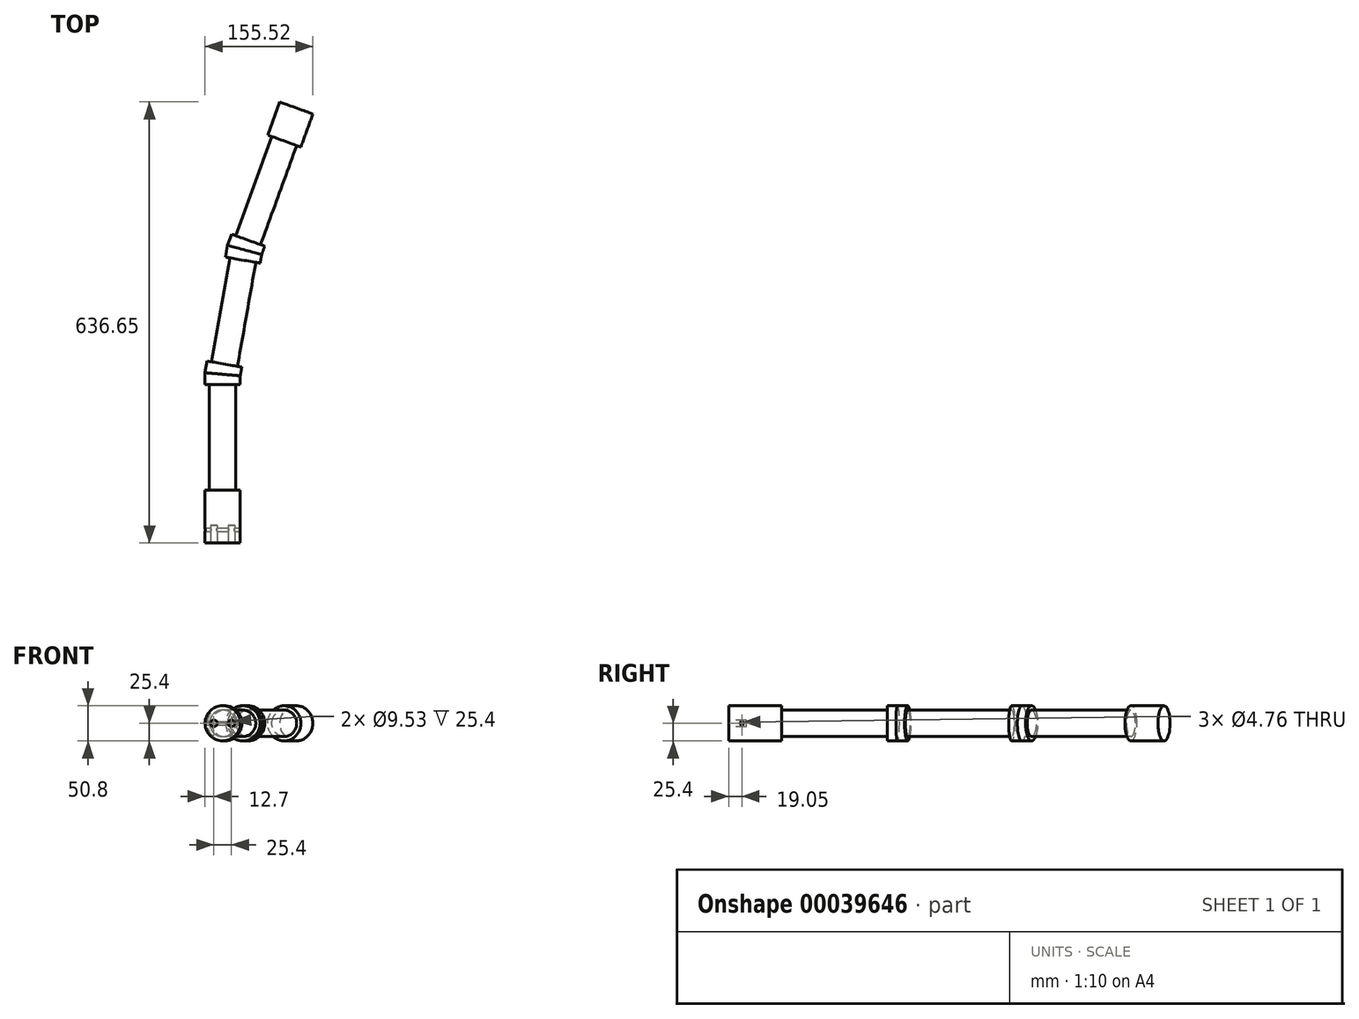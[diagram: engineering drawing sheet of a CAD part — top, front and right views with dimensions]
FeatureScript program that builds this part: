
annotation { "Feature Type Name" : "Feature", "Feature Type Description" : "" }
export const myFeature = defineFeature(function(context is Context, id is Id, definition is map)
    precondition{}
    {
        {
            var Q0;
            Q0=qCreatedBy(makeId("Top.planeOp"),FACE);
            var sketch = newSketch(context, id + "F0", { "sketchPlane" : qUnion([Q0])});
            skLineSegment(sketch, "E0", {"start": v(0, 0) * mm, "end": v(-19.05, 0) * mm});
            skLineSegment(sketch, "E1", {"start": v(0, 0) * mm, "end": v(19.05, 0) * mm});
            skLineSegment(sketch, "E2", {"start": v(19.05, 0) * mm, "end": v(19.05, 152.4) * mm});
            skLineSegment(sketch, "E3", {"start": v(-19.05, 0) * mm, "end": v(-19.05, 152.4) * mm});
            skLineSegment(sketch, "E4", {"start": v(-19.05, 152.4) * mm, "end": v(19.05, 152.4) * mm});
            skLineSegment(sketch, "E5", {"start": v(19.05, 152.4) * mm, "end": v(25.4, 152.4) * mm});
            skLineSegment(sketch, "E6", {"start": v(25.4, 152.4) * mm, "end": v(25.4, 165.1) * mm});
            skLineSegment(sketch, "E7", {"start": v(25.4, 165.1) * mm, "end": v(27.6, 177.6) * mm});
            skLineSegment(sketch, "E8", {"start": v(-19.05, 152.4) * mm, "end": v(-25.4, 152.4) * mm});
            skLineSegment(sketch, "E9", {"start": v(27.6, 177.6) * mm, "end": v(-22.42, 186.43) * mm});
            skLineSegment(sketch, "E10", {"start": v(25.4, 165.1) * mm, "end": v(-25.4, 169.54) * mm});
            skLineSegment(sketch, "E11", {"start": v(-25.4, 152.4) * mm, "end": v(-25.4, 169.54) * mm});
            skLineSegment(sketch, "E12", {"start": v(-25.4, 169.54) * mm, "end": v(-22.42, 186.43) * mm});
            skLineSegment(sketch, "E13", {"start": v(27.6, 177.6) * mm, "end": v(21.35, 178.7) * mm});
            skLineSegment(sketch, "E14", {"start": v(21.35, 178.7) * mm, "end": v(47.82, 328.8) * mm});
            skLineSegment(sketch, "E15", {"start": v(47.82, 328.8) * mm, "end": v(10.3, 335.41) * mm});
            skLineSegment(sketch, "E16", {"start": v(10.3, 335.41) * mm, "end": v(-16.17, 185.33) * mm});
            skLineSegment(sketch, "E17", {"start": v(47.82, 328.8) * mm, "end": v(54.07, 327.7) * mm});
            skLineSegment(sketch, "E18", {"start": v(54.07, 327.7) * mm, "end": v(56.27, 340.2) * mm});
            skLineSegment(sketch, "E19", {"start": v(10.3, 335.41) * mm, "end": v(4.04, 336.51) * mm});
            skLineSegment(sketch, "E20", {"start": v(56.27, 340.2) * mm, "end": v(60.62, 352.13) * mm});
            skLineSegment(sketch, "E21", {"start": v(60.62, 352.13) * mm, "end": v(12.88, 369.5) * mm});
            skLineSegment(sketch, "E22", {"start": v(56.27, 340.2) * mm, "end": v(7.02, 353.4) * mm});
            skLineSegment(sketch, "E23", {"start": v(4.04, 336.51) * mm, "end": v(7.02, 353.4) * mm});
            skLineSegment(sketch, "E24", {"start": v(7.02, 353.4) * mm, "end": v(12.88, 369.5) * mm});
            skLineSegment(sketch, "E25", {"start": v(60.62, 352.13) * mm, "end": v(54.65, 354.3) * mm});
            skLineSegment(sketch, "E26", {"start": v(19.05, 0) * mm, "end": v(25.4, 0) * mm});
            skLineSegment(sketch, "E27", {"start": v(25.4, 0) * mm, "end": v(25.4, -50.8) * mm});
            skLineSegment(sketch, "E28", {"start": v(25.4, -50.8) * mm, "end": v(-25.4, -50.8) * mm});
            skLineSegment(sketch, "E29", {"start": v(-25.4, -50.8) * mm, "end": v(-25.4, 0) * mm});
            skLineSegment(sketch, "E30", {"start": v(-25.4, 0) * mm, "end": v(-19.05, 0) * mm});
            skLineSegment(sketch, "E31", {"start": v(54.65, 354.3) * mm, "end": v(106.78, 497.51) * mm});
            skLineSegment(sketch, "E32", {"start": v(106.78, 497.51) * mm, "end": v(112.74, 495.34) * mm});
            skLineSegment(sketch, "E33", {"start": v(130.12, 543.08) * mm, "end": v(82.38, 560.45) * mm});
            skLineSegment(sketch, "E34", {"start": v(70.97, 510.54) * mm, "end": v(18.85, 367.34) * mm});
            skLineSegment(sketch, "E35", {"start": v(70.97, 510.54) * mm, "end": v(106.78, 497.51) * mm});
            skLineSegment(sketch, "E36", {"start": v(130.12, 543.08) * mm, "end": v(112.74, 495.34) * mm});
            skLineSegment(sketch, "E37", {"start": v(82.38, 560.45) * mm, "end": v(65, 512.72) * mm});
            skLineSegment(sketch, "E38", {"start": v(65, 512.72) * mm, "end": v(70.97, 510.54) * mm});
            skSolve(sketch);
        }
        {
            var Q0;
            Q0=makeQuery(id+"F0.imprint","IMPRINT",FACE,{"disambiguationData":[TD([[makeQuery(id+"F0.imprint","IMPRINT",EDGE,{"derivedFrom":sQuery(id+"F0.wireOp",EDGE,"E20")}),1.0]])]});
            var Q1;
            Q1=makeQuery(id+"F0.imprint","IMPRINT",FACE,{"disambiguationData":[TD([[makeQuery(id+"F0.imprint","IMPRINT",EDGE,{"derivedFrom":sQuery(id+"F0.wireOp",EDGE,"E15")}),-1.0]])]});
            var Q2;
            Q2=makeQuery(id+"F0.imprint","IMPRINT",FACE,{"disambiguationData":[TD([[makeQuery(id+"F0.imprint","IMPRINT",EDGE,{"derivedFrom":sQuery(id+"F0.wireOp",EDGE,"E7")}),1.0]])]});
            var Q3;
            Q3=makeQuery(id+"F0.imprint","IMPRINT",FACE,{"disambiguationData":[TD([[makeQuery(id+"F0.imprint","IMPRINT",EDGE,{"derivedFrom":sQuery(id+"F0.wireOp",EDGE,"E4")}),1.0]])]});
            var Q4;
            Q4=makeQuery(id+"F0.imprint","IMPRINT",FACE,{"disambiguationData":[TD([[makeQuery(id+"F0.imprint","IMPRINT",EDGE,{"derivedFrom":sQuery(id+"F0.wireOp",EDGE,"E0")}),1.0]])]});
            var Q5;
            Q5=makeQuery(id+"F0.imprint","IMPRINT",FACE,{"disambiguationData":[TD([[makeQuery(id+"F0.imprint","IMPRINT",EDGE,{"derivedFrom":sQuery(id+"F0.wireOp",EDGE,"4362853a-bfab-4841-ad33-0da4945ce7d8")}),-1.0]])]});
            var Q6;
            Q6=makeQuery(id+"F0.imprint","IMPRINT",FACE,{"disambiguationData":[TD([[makeQuery(id+"F0.imprint","IMPRINT",EDGE,{"derivedFrom":sQuery(id+"F0.wireOp",EDGE,"9ec19a48-1b8f-4e76-9588-66d74d53f144")}),-1.0]])]});
            var Q7;
            Q7=makeQuery(id+"F0.imprint","IMPRINT",FACE,{"disambiguationData":[TD([[makeQuery(id+"F0.imprint","IMPRINT",EDGE,{"derivedFrom":sQuery(id+"F0.wireOp",EDGE,"E32")}),1.0]])]});
            var Q8;
            Q8=makeQuery(id+"F0.imprint","IMPRINT",FACE,{"disambiguationData":[TD([[makeQuery(id+"F0.imprint","IMPRINT",EDGE,{"derivedFrom":sQuery(id+"F0.wireOp",EDGE,"134bd195-3179-4c87-b82c-456532974db7")}),1.0]])]});
            var Q9;
            Q9=makeQuery(id+"F0.imprint","IMPRINT",FACE,{"disambiguationData":[TD([[makeQuery(id+"F0.imprint","IMPRINT",EDGE,{"derivedFrom":sQuery(id+"F0.wireOp",EDGE,"030bf412-2708-412a-a3c6-39b4ca16a0eb")}),1.0]])]});
            var Q10;
            Q10=makeQuery(id+"F0.imprint","IMPRINT",FACE,{"disambiguationData":[TD([[makeQuery(id+"F0.imprint","IMPRINT",EDGE,{"derivedFrom":sQuery(id+"F0.wireOp",EDGE,"134bd195-3179-4c87-b82c-456532974db7")}),-1.0]])]});
            var Q11;
            Q11=makeQuery(id+"F0.imprint","IMPRINT",FACE,{"disambiguationData":[TD([[makeQuery(id+"F0.imprint","IMPRINT",EDGE,{"derivedFrom":sQuery(id+"F0.wireOp",EDGE,"E33")}),-1.0]])]});
            var Q12;
            Q12=makeQuery(id+"F0.imprint","IMPRINT",FACE,{"disambiguationData":[TD([[makeQuery(id+"F0.imprint","IMPRINT",EDGE,{"derivedFrom":sQuery(id+"F0.wireOp",EDGE,"e989e8fa-5b56-48d0-8351-93b8a3e71791")}),-1.0]])]});
            extrude(context, id + "F1", {"entities" : qUnion([Q0, Q1, Q2, Q3, Q4, Q5, Q6, Q7, Q8, Q9, Q10, Q11, Q12]), "endBound" : BoundingType.SYMMETRIC, "depth" : 50.8 * mm});
        }
        {
            var Q0;
            {var subQ1=sQuery(id+"F0.wireOp",EDGE,"E31");Q0=makeQuery(id+"F0.imprint","IMPRINT",FACE,{"disambiguationData":[TD([[makeQuery(id+"F0.imprint","IMPRINT",EDGE,{"derivedFrom":subQ1}),1.0]])]});}
            var Q1;
            {var subQ1=sQuery(id+"F0.wireOp",EDGE,"E14");Q1=makeQuery(id+"F0.imprint","IMPRINT",FACE,{"disambiguationData":[TD([[makeQuery(id+"F0.imprint","IMPRINT",EDGE,{"derivedFrom":subQ1}),1.0]])]});}
            var Q2;
            Q2=makeQuery(id+"F0.imprint","IMPRINT",FACE,{"disambiguationData":[TD([[makeQuery(id+"F0.imprint","IMPRINT",EDGE,{"derivedFrom":sQuery(id+"F0.wireOp",EDGE,"E0")}),-1.0]])]});
            extrude(context, id + "F2", {"entities" : qUnion([Q0, Q1, Q2]), "endBound" : BoundingType.SYMMETRIC, "depth" : 38.1 * mm});
        }
        {
            var Q0;
            Q0=makeQuery(id+"F2.opExtrude","CAP_EDGE",EDGE,{"disambiguationData":[OSD([sQuery(id+"F0.wireOp",EDGE,"E31")])],"isStart":false});
            var Q1;
            Q1=makeQuery(id+"F2.opExtrude","CAP_EDGE",EDGE,{"disambiguationData":[OSD([sQuery(id+"F0.wireOp",EDGE,"E34")])],"isStart":false});
            var Q2;
            Q2=makeQuery(id+"F2.opExtrude","CAP_EDGE",EDGE,{"disambiguationData":[OSD([sQuery(id+"F0.wireOp",EDGE,"E14")])],"isStart":false});
            var Q3;
            Q3=makeQuery(id+"F2.opExtrude","CAP_EDGE",EDGE,{"disambiguationData":[OSD([sQuery(id+"F0.wireOp",EDGE,"E16")])],"isStart":false});
            var Q4;
            Q4=makeQuery(id+"F2.opExtrude","CAP_EDGE",EDGE,{"disambiguationData":[OSD([sQuery(id+"F0.wireOp",EDGE,"E2")])],"isStart":false});
            var Q5;
            Q5=makeQuery(id+"F2.opExtrude","CAP_EDGE",EDGE,{"disambiguationData":[OSD([sQuery(id+"F0.wireOp",EDGE,"E3")])],"isStart":false});
            var Q6;
            Q6=makeQuery(id+"F2.opExtrude","CAP_EDGE",EDGE,{"disambiguationData":[OSD([sQuery(id+"F0.wireOp",EDGE,"E2")])],"isStart":true});
            var Q7;
            Q7=makeQuery(id+"F2.opExtrude","CAP_EDGE",EDGE,{"disambiguationData":[OSD([sQuery(id+"F0.wireOp",EDGE,"E3")])],"isStart":true});
            var Q8;
            Q8=makeQuery(id+"F2.opExtrude","CAP_EDGE",EDGE,{"disambiguationData":[OSD([sQuery(id+"F0.wireOp",EDGE,"E14")])],"isStart":true});
            var Q9;
            Q9=makeQuery(id+"F2.opExtrude","CAP_EDGE",EDGE,{"disambiguationData":[OSD([sQuery(id+"F0.wireOp",EDGE,"E16")])],"isStart":true});
            var Q10;
            Q10=makeQuery(id+"F2.opExtrude","CAP_EDGE",EDGE,{"disambiguationData":[OSD([sQuery(id+"F0.wireOp",EDGE,"E31")])],"isStart":true});
            var Q11;
            Q11=makeQuery(id+"F2.opExtrude","CAP_EDGE",EDGE,{"disambiguationData":[OSD([sQuery(id+"F0.wireOp",EDGE,"E34")])],"isStart":true});
            fillet(context, id + "F3", {"entities" : qUnion([Q0, Q1, Q2, Q3, Q4, Q5, Q6, Q7, Q8, Q9, Q10, Q11]), "radius" : 19.05 * mm, "tangentPropagation" : true, "allowEdgeOverflow" : false});
        }
        {
            var Q0;
            Q0=makeQuery(id+"F1.opExtrude","CAP_EDGE",EDGE,{"disambiguationData":[OSD([sQuery(id+"F0.wireOp",EDGE,"E7")])],"isStart":false});
            var Q1;
            Q1=makeQuery(id+"F1.opExtrude","CAP_EDGE",EDGE,{"disambiguationData":[OSD([sQuery(id+"F0.wireOp",EDGE,"E12")])],"isStart":false});
            var Q2;
            Q2=makeQuery(id+"F1.opExtrude","CAP_EDGE",EDGE,{"disambiguationData":[OSD([sQuery(id+"F0.wireOp",EDGE,"E11")])],"isStart":false});
            var Q3;
            Q3=makeQuery(id+"F1.opExtrude","CAP_EDGE",EDGE,{"disambiguationData":[OSD([sQuery(id+"F0.wireOp",EDGE,"E6")])],"isStart":false});
            var Q4;
            Q4=makeQuery(id+"F1.opExtrude","CAP_EDGE",EDGE,{"disambiguationData":[OSD([sQuery(id+"F0.wireOp",EDGE,"E7")])],"isStart":true});
            var Q5;
            Q5=makeQuery(id+"F1.opExtrude","CAP_EDGE",EDGE,{"disambiguationData":[OSD([sQuery(id+"F0.wireOp",EDGE,"E6")])],"isStart":true});
            var Q6;
            Q6=makeQuery(id+"F1.opExtrude","CAP_EDGE",EDGE,{"disambiguationData":[OSD([sQuery(id+"F0.wireOp",EDGE,"E11")])],"isStart":true});
            var Q7;
            Q7=makeQuery(id+"F1.opExtrude","CAP_EDGE",EDGE,{"disambiguationData":[OSD([sQuery(id+"F0.wireOp",EDGE,"E12")])],"isStart":true});
            var Q8;
            Q8=makeQuery(id+"F1.opExtrude","CAP_EDGE",EDGE,{"disambiguationData":[OSD([sQuery(id+"F0.wireOp",EDGE,"E23")])],"isStart":true});
            var Q9;
            Q9=makeQuery(id+"F1.opExtrude","CAP_EDGE",EDGE,{"disambiguationData":[OSD([sQuery(id+"F0.wireOp",EDGE,"E24")])],"isStart":true});
            var Q10;
            Q10=makeQuery(id+"F1.opExtrude","CAP_EDGE",EDGE,{"disambiguationData":[OSD([sQuery(id+"F0.wireOp",EDGE,"E18")])],"isStart":true});
            var Q11;
            Q11=makeQuery(id+"F1.opExtrude","CAP_EDGE",EDGE,{"disambiguationData":[OSD([sQuery(id+"F0.wireOp",EDGE,"E20")])],"isStart":true});
            var Q12;
            Q12=makeQuery(id+"F1.opExtrude","CAP_EDGE",EDGE,{"disambiguationData":[OSD([sQuery(id+"F0.wireOp",EDGE,"E20")])],"isStart":false});
            var Q13;
            Q13=makeQuery(id+"F1.opExtrude","CAP_EDGE",EDGE,{"disambiguationData":[OSD([sQuery(id+"F0.wireOp",EDGE,"E24")])],"isStart":false});
            var Q14;
            Q14=makeQuery(id+"F1.opExtrude","CAP_EDGE",EDGE,{"disambiguationData":[OSD([sQuery(id+"F0.wireOp",EDGE,"E23")])],"isStart":false});
            var Q15;
            Q15=makeQuery(id+"F1.opExtrude","CAP_EDGE",EDGE,{"disambiguationData":[OSD([sQuery(id+"F0.wireOp",EDGE,"E18")])],"isStart":false});
            var Q16;
            Q16=makeQuery(id+"F1.opExtrude","CAP_EDGE",EDGE,{"disambiguationData":[OSD([sQuery(id+"F0.wireOp",EDGE,"E36")])],"isStart":false});
            var Q17;
            Q17=makeQuery(id+"F1.opExtrude","CAP_EDGE",EDGE,{"disambiguationData":[OSD([sQuery(id+"F0.wireOp",EDGE,"E36")])],"isStart":true});
            var Q18;
            Q18=makeQuery(id+"F1.opExtrude","CAP_EDGE",EDGE,{"disambiguationData":[OSD([sQuery(id+"F0.wireOp",EDGE,"E37")])],"isStart":false});
            var Q19;
            Q19=makeQuery(id+"F1.opExtrude","CAP_EDGE",EDGE,{"disambiguationData":[OSD([sQuery(id+"F0.wireOp",EDGE,"E37")])],"isStart":true});
            var Q20;
            Q20=makeQuery(id+"F1.opExtrude","CAP_EDGE",EDGE,{"disambiguationData":[OSD([sQuery(id+"F0.wireOp",EDGE,"e989e8fa-5b56-48d0-8351-93b8a3e71791")])],"isStart":false});
            var Q21;
            Q21=makeQuery(id+"F1.opExtrude","CAP_EDGE",EDGE,{"disambiguationData":[OSD([sQuery(id+"F0.wireOp",EDGE,"134bd195-3179-4c87-b82c-456532974db7")])],"isStart":false});
            var Q22;
            Q22=makeQuery(id+"F1.opExtrude","CAP_EDGE",EDGE,{"disambiguationData":[OSD([sQuery(id+"F0.wireOp",EDGE,"24408120-6648-494d-915d-874de320521e"),sQuery(id+"F0.wireOp",EDGE,"286c20bf-4efd-40d8-b315-46f60f12ca12"),sQuery(id+"F0.wireOp",EDGE,"3496fda2-568e-4d73-ae0b-d68eb73aed0e")])],"isStart":false});
            var Q23;
            Q23=makeQuery(id+"F1.opExtrude","CAP_EDGE",EDGE,{"disambiguationData":[OSD([sQuery(id+"F0.wireOp",EDGE,"134bd195-3179-4c87-b82c-456532974db7")])],"isStart":true});
            var Q24;
            Q24=makeQuery(id+"F1.opExtrude","CAP_EDGE",EDGE,{"disambiguationData":[OSD([sQuery(id+"F0.wireOp",EDGE,"e989e8fa-5b56-48d0-8351-93b8a3e71791")])],"isStart":true});
            var Q25;
            Q25=makeQuery(id+"F1.opExtrude","CAP_EDGE",EDGE,{"disambiguationData":[OSD([sQuery(id+"F0.wireOp",EDGE,"24408120-6648-494d-915d-874de320521e"),sQuery(id+"F0.wireOp",EDGE,"286c20bf-4efd-40d8-b315-46f60f12ca12"),sQuery(id+"F0.wireOp",EDGE,"3496fda2-568e-4d73-ae0b-d68eb73aed0e")])],"isStart":true});
            fillet(context, id + "F4", {"entities" : qUnion([Q0, Q1, Q2, Q3, Q4, Q5, Q6, Q7, Q8, Q9, Q10, Q11, Q12, Q13, Q14, Q15, Q16, Q17, Q18, Q19, Q20, Q21, Q22, Q23, Q24, Q25]), "radius" : 25.4 * mm, "tangentPropagation" : true, "allowEdgeOverflow" : false});
        }
        {
            var Q0;
            Q0=makeQuery(id+"F1.opExtrude","CAP_EDGE",EDGE,{"disambiguationData":[OSD([sQuery(id+"F0.wireOp",EDGE,"4362853a-bfab-4841-ad33-0da4945ce7d8")])],"isStart":false});
            var Q1;
            Q1=makeQuery(id+"F1.opExtrude","CAP_EDGE",EDGE,{"disambiguationData":[OSD([sQuery(id+"F0.wireOp",EDGE,"4362853a-bfab-4841-ad33-0da4945ce7d8")])],"isStart":true});
            var Q2;
            Q2=makeQuery(id+"F1.opExtrude","CAP_EDGE",EDGE,{"disambiguationData":[OSD([sQuery(id+"F0.wireOp",EDGE,"9ec19a48-1b8f-4e76-9588-66d74d53f144")])],"isStart":false});
            var Q3;
            Q3=makeQuery(id+"F1.opExtrude","CAP_EDGE",EDGE,{"disambiguationData":[OSD([sQuery(id+"F0.wireOp",EDGE,"9ec19a48-1b8f-4e76-9588-66d74d53f144")])],"isStart":true});
            var Q4;
            Q4=makeQuery(id+"F1.opExtrude","CAP_EDGE",EDGE,{"disambiguationData":[OSD([sQuery(id+"F0.wireOp",EDGE,"E29")])],"isStart":true});
            var Q5;
            Q5=makeQuery(id+"F1.opExtrude","CAP_EDGE",EDGE,{"disambiguationData":[OSD([sQuery(id+"F0.wireOp",EDGE,"E27")])],"isStart":true});
            var Q6;
            Q6=makeQuery(id+"F1.opExtrude","CAP_EDGE",EDGE,{"disambiguationData":[OSD([sQuery(id+"F0.wireOp",EDGE,"E29")])],"isStart":false});
            var Q7;
            Q7=makeQuery(id+"F1.opExtrude","CAP_EDGE",EDGE,{"disambiguationData":[OSD([sQuery(id+"F0.wireOp",EDGE,"E27")])],"isStart":false});
            fillet(context, id + "F5", {"entities" : qUnion([Q0, Q1, Q2, Q3, Q4, Q5, Q6, Q7]), "radius" : 25.4 * mm, "tangentPropagation" : true, "allowEdgeOverflow" : false});
        }
        {
            var Q0;
            Q0=makeQuery(id+"F1.opExtrude","SWEPT_FACE",FACE,{"disambiguationData":[OSD([sQuery(id+"F0.wireOp",EDGE,"E28")])]});
            extrude(context, id + "F6", {"entities" : qUnion([Q0]), "operationType" : NewBodyOperationType.ADD, "depth" : 25.4 * mm});
        }
        {
            var Q0;
            Q0=makeQuery(id+"F6.opExtrude","CAP_FACE",FACE,{"disambiguationData":[OSD([sQuery(id+"F0.wireOp",EDGE,"E28")])],"isStart":false});
            var sketch = newSketch(context, id + "F7", { "sketchPlane" : qUnion([Q0])});
            skLineSegment(sketch, "E39", {"start": v(0, -25.4) * mm, "end": v(0, 25.4) * mm});
            skArc(sketch, "E40", {"start": v(0, 25.4) * mm, "mid": v(-24.57, 0) * mm, "end": v(0, -25.4) * mm});
            skSolve(sketch);
        }
        {
            var Q0;
            {var subQ1=sQuery(id+"F7.wireOp",EDGE,"E39");Q0=makeQuery(id+"F7.imprint","IMPRINT",FACE,{"disambiguationData":[TD([[makeQuery(id+"F7.imprint","IMPRINT",EDGE,{"derivedFrom":subQ1}),-1.0]])]});}
            var sketch = newSketch(context, id + "F8", { "sketchPlane" : qUnion([Q0])});
            skLineSegment(sketch, "E41", {"start": v(0, 0) * mm, "end": v(12.7, 0) * mm});
            skLineSegment(sketch, "E42", {"start": v(0, 0) * mm, "end": v(-12.7, 0) * mm});
            skCircle(sketch, "E43", {"center": v(12.7, 0) * mm, "radius": 4.76 * mm});
            skCircle(sketch, "E44", {"center": v(-12.7, 0) * mm, "radius": 4.76 * mm});
            skSolve(sketch);
        }
        {
            var Q0;
            Q0=makeQuery(id+"F8.imprint","IMPRINT",FACE,{"disambiguationData":[TD([[makeQuery(id+"F8.imprint","IMPRINT",EDGE,{"derivedFrom":sQuery(id+"F8.wireOp",EDGE,"E44")}),1.0]])]});
            var Q1;
            Q1=makeQuery(id+"F8.imprint","IMPRINT",FACE,{"disambiguationData":[TD([[makeQuery(id+"F8.imprint","IMPRINT",EDGE,{"derivedFrom":sQuery(id+"F8.wireOp",EDGE,"E43")}),1.0]])]});
            extrude(context, id + "F9", {"entities" : qUnion([Q0, Q1]), "operationType" : NewBodyOperationType.REMOVE, "oppositeDirection" : true, "depth" : 25.4 * mm});
        }
        {
            var Q0;
            Q0=qCreatedBy(makeId("Right.planeOp"),FACE);
            var sketch = newSketch(context, id + "F10", { "sketchPlane" : qUnion([Q0])});
            skCircle(sketch, "E45", {"center": v(-57.15, 0) * mm, "radius": 2.38 * mm});
            skLineSegment(sketch, "E46", {"start": v(-76.2, 25.4) * mm, "end": v(0, 25.4) * mm});
            skLineSegment(sketch, "E47.0", {"start": v(-76.2, -25.4) * mm, "end": v(-76.2, 25.4) * mm});
            skLineSegment(sketch, "E48", {"start": v(-57.15, 0) * mm, "end": v(-76.2, 0) * mm});
            skSolve(sketch);
        }
        {
            var Q0;
            Q0=makeQuery(id+"F10.imprint","IMPRINT",FACE,{"disambiguationData":[TD([[makeQuery(id+"F10.imprint","IMPRINT",EDGE,{"derivedFrom":sQuery(id+"F10.wireOp",EDGE,"E45")}),1.0]])]});
            extrude(context, id + "F11", {"entities" : qUnion([Q0]), "operationType" : NewBodyOperationType.REMOVE, "endBound" : BoundingType.SYMMETRIC, "oppositeDirection" : true, "depth" : 50.8 * mm});
        }
    });
